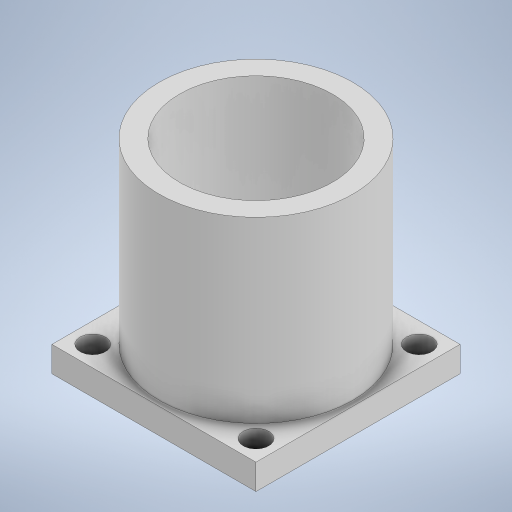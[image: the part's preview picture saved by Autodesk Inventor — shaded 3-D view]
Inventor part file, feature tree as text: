
AUTODESK INVENTOR PART (.ipt)
format: ipt  version: 2023 (Build 270158000, 158)  size: 235,008 bytes
history: native  units: in
note: dims shown in document units (in); Inventor stores cm internally (conversion verified against a paired STEP export)
features: extrude x3, sketch x1
ambient origin geometry x8: Origin, YZ Plane, XZ Plane, XY Plane, X Axis, Y Axis, Z Axis, Center Point
bodies: Solid1 (feature_tree)
feature tree (4):
  sketch  "Sketch1"  dims[d6=2.0in d7=0.0in d10=2.0in d11=2.0in d12=0.25in d13=0.0in d20=0.25in d23=0.25in d24=0.0in]
  extrude  "Extrusion1"  Depth=2.0in
  extrude  "Extrusion3"  Depth=2.0in
  extrude  "Extrusion5"  Depth=0.25in TaperAngle=0.0deg
